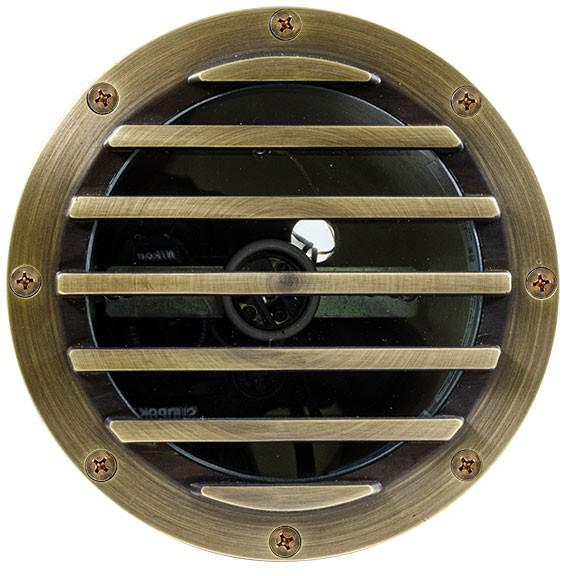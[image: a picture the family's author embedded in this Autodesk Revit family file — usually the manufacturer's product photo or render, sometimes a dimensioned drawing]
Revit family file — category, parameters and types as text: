
# Revit family: Alcon-9043-Revit-Family
name_source: partatom
category: Luminarias
units: mm (PartAtom-declared; Revit-internal decimal feet)

## family parameters
Anfitrión = Cara
Compartido = No
Corte con vacíos al cargar = No
Cota de conector redondo = Usar diámetro
Mantener orientación de anotación = No
Origen de luz = Sí
Punto de cálculo de habitación = No
Tipo de pieza = Normal

## types (1)
- Alcon-9043-Revit-Family
    Cambio de temperatura de color de luz atenuada = <Ninguno>
    Elevación por defecto = 4' - 0"
    Fabricante = Alcon Lighting
    Filtro de color = 16777215
    GLASS LENS = Analytical Panels
    HOUSING = <Por categoría>
    LENS GLASS = Glass
    Link to IES File = https://www.alconlighting.com
    Longitud de símbolo de origen de luz = 10' - 0"
    Modelo = Alcon Lighting 9043
    Product Data URL = https://www.alconlighting.com
    Product Page = https://www.alconlighting.com
    TAP LENS = <Por categoría>
    TOP FINISH = <Por categoría>
    URL = https://www.alconlighting.com
    Ángulo de campo de foco = 90.00°
    Ángulo de enfoque = 30.00°
    Ángulo de inclinación = 60.00°

## geometry (parser evidence)
native form markers: Sweep x3
no freeform markers — native parametric forms only
